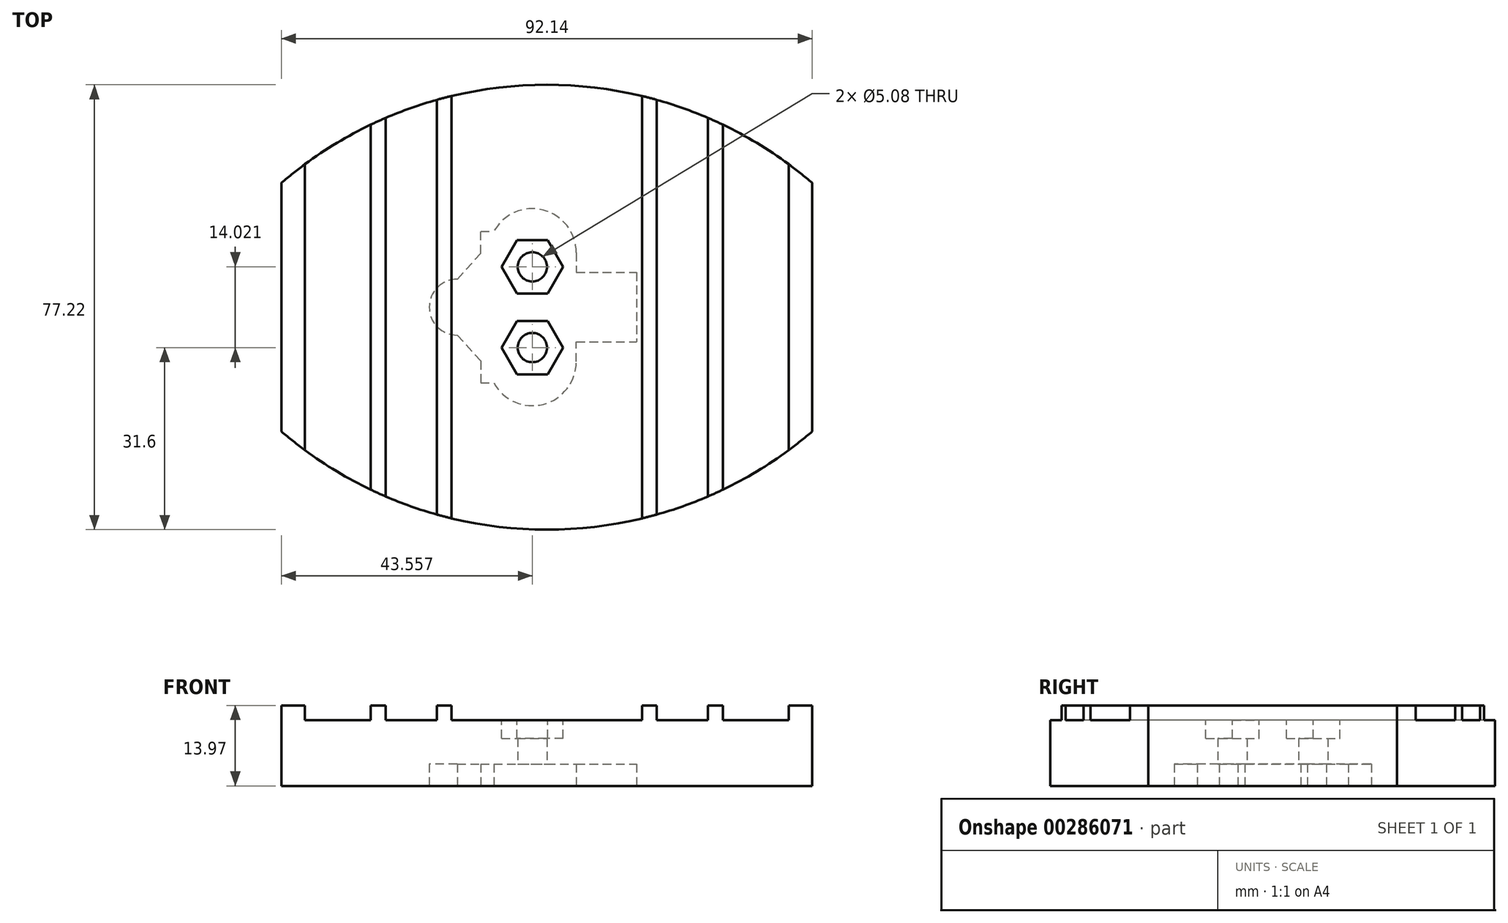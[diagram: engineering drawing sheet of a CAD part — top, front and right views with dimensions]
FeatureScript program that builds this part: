
annotation { "Feature Type Name" : "Feature", "Feature Type Description" : "" }
export const myFeature = defineFeature(function(context is Context, id is Id, definition is map)
    precondition{}
    {
        {
            var Q0;
            Q0=qCreatedBy(makeId("Top.planeOp"),FACE);
            var sketch = newSketch(context, id + "F0", { "sketchPlane" : qUnion([Q0])});
            skLineSegment(sketch, "E0.bottom", {"start": v(46.07, 38.6) * mm, "end": v(-46.07, 38.6) * mm});
            skLineSegment(sketch, "E0.top", {"start": v(46.07, -38.6) * mm, "end": v(-46.07, -38.6) * mm});
            skLineSegment(sketch, "E0.left", {"start": v(46.07, 38.6) * mm, "end": v(46.07, -38.6) * mm});
            skLineSegment(sketch, "E0.right", {"start": v(-46.07, 38.6) * mm, "end": v(-46.07, -38.6) * mm});
            skPoint(sketch, "E0.middle", {"position": v(0, 0) * mm});
            skSolve(sketch);
        }
        {
            var Q0;
            Q0=makeQuery(id+"F0.imprint","IMPRINT",FACE,{"disambiguationData":[TD([[makeQuery(id+"F0.imprint","IMPRINT",EDGE,{"derivedFrom":sQuery(id+"F0.wireOp",EDGE,"E0.bottom")}),1.0]])]});
            extrude(context, id + "F1", {"entities" : qUnion([Q0]), "depth" : 13.97 * mm, "offsetDistance" : 25.4 * mm});
        }
        {
            var Q0;
            Q0=makeQuery(id+"F1.opExtrude","CAP_FACE",FACE,{"disambiguationData":[OSD([sQuery(id+"F0.wireOp",EDGE,"E0.bottom"),sQuery(id+"F0.wireOp",EDGE,"E0.top"),sQuery(id+"F0.wireOp",EDGE,"E0.left"),sQuery(id+"F0.wireOp",EDGE,"E0.right")])],"isStart":false});
            var sketch = newSketch(context, id + "F2", { "sketchPlane" : qUnion([Q0])});
            skLineSegment(sketch, "E1", {"start": v(0, -4.16) * mm, "end": v(0, -123.72) * mm, "construction": true});
            skArc(sketch, "E2", {"start": v(46.07, 21.59) * mm, "mid": v(0, 38.6) * mm, "end": v(-46.07, 21.6) * mm});
            skLineSegment(sketch, "E3", {"start": v(46.07, 0) * mm, "end": v(46.07, 21.59) * mm});
            skPoint(sketch, "E4", {"position": v(-46.07, 21.6) * mm});
            skLineSegment(sketch, "E5", {"start": v(0, -4.16) * mm, "end": v(0, 108.32) * mm, "construction": true});
            skArc(sketch, "E6", {"start": v(-46.07, -21.59) * mm, "mid": v(0, -38.6) * mm, "end": v(46.07, -21.6) * mm});
            skLineSegment(sketch, "E7", {"start": v(-46.07, 0) * mm, "end": v(-46.07, -21.6) * mm});
            skPoint(sketch, "E8", {"position": v(46.07, -21.6) * mm});
            skLineSegment(sketch, "E9", {"start": v(-46.07, 0) * mm, "end": v(-46.07, 21.6) * mm});
            skLineSegment(sketch, "E10", {"start": v(46.07, 0) * mm, "end": v(46.07, -21.6) * mm});
            skSolve(sketch);
        }
        {
            var Q0;
            Q0 = qSketchRegion(id + "F2", true);
            extrude(context, id + "F3", {"entities" : qUnion([Q0]), "operationType" : NewBodyOperationType.INTERSECT, "endBound" : BoundingType.THROUGH_ALL, "oppositeDirection" : true, "depth" : 25.4 * mm});
        }
        {
            var Q0;
            Q0=qCreatedBy(makeId("Front.planeOp"),FACE);
            var sketch = newSketch(context, id + "F4", { "sketchPlane" : qUnion([Q0])});
            skLineSegment(sketch, "E11.bottom", {"start": v(-42, 13.97) * mm, "end": v(-30.57, 13.97) * mm});
            skLineSegment(sketch, "E11.top", {"start": v(-42, 11.43) * mm, "end": v(-30.57, 11.43) * mm});
            skLineSegment(sketch, "E11.left", {"start": v(-42, 13.97) * mm, "end": v(-42, 11.43) * mm});
            skLineSegment(sketch, "E11.right", {"start": v(-30.57, 13.97) * mm, "end": v(-30.57, 11.43) * mm});
            skLineSegment(sketch, "E12.bottom", {"start": v(-27.99, 13.97) * mm, "end": v(-19.1, 13.97) * mm});
            skLineSegment(sketch, "E12.top", {"start": v(-27.99, 11.43) * mm, "end": v(-19.1, 11.43) * mm});
            skLineSegment(sketch, "E12.left", {"start": v(-27.99, 13.97) * mm, "end": v(-27.99, 11.43) * mm});
            skLineSegment(sketch, "E12.right", {"start": v(-19.1, 13.97) * mm, "end": v(-19.1, 11.43) * mm});
            skLineSegment(sketch, "E13.bottom", {"start": v(-16.51, 13.97) * mm, "end": v(16.51, 13.97) * mm});
            skLineSegment(sketch, "E13.top", {"start": v(-16.51, 11.43) * mm, "end": v(16.51, 11.43) * mm});
            skLineSegment(sketch, "E13.left", {"start": v(-16.51, 13.97) * mm, "end": v(-16.51, 11.43) * mm});
            skLineSegment(sketch, "E13.right", {"start": v(16.51, 13.97) * mm, "end": v(16.51, 11.43) * mm});
            skLineSegment(sketch, "E14.bottom", {"start": v(19.1, 13.97) * mm, "end": v(27.99, 13.97) * mm});
            skLineSegment(sketch, "E14.top", {"start": v(19.1, 11.43) * mm, "end": v(27.99, 11.43) * mm});
            skLineSegment(sketch, "E14.left", {"start": v(19.1, 13.97) * mm, "end": v(19.1, 11.43) * mm});
            skLineSegment(sketch, "E14.right", {"start": v(27.99, 13.97) * mm, "end": v(27.99, 11.43) * mm});
            skLineSegment(sketch, "E15.bottom", {"start": v(30.57, 13.97) * mm, "end": v(42, 13.97) * mm});
            skLineSegment(sketch, "E15.top", {"start": v(30.57, 11.43) * mm, "end": v(42, 11.43) * mm});
            skLineSegment(sketch, "E15.left", {"start": v(30.57, 13.97) * mm, "end": v(30.57, 11.43) * mm});
            skLineSegment(sketch, "E15.right", {"start": v(42, 13.97) * mm, "end": v(42, 11.43) * mm});
            skLineSegment(sketch, "E16", {"start": v(0, 11.43) * mm, "end": v(0, 0) * mm});
            skLineSegment(sketch, "E17", {"start": v(-30.57, 12.7) * mm, "end": v(-27.99, 12.7) * mm});
            skLineSegment(sketch, "E18", {"start": v(-19.1, 12.7) * mm, "end": v(-16.51, 12.7) * mm});
            skLineSegment(sketch, "E19", {"start": v(16.51, 12.7) * mm, "end": v(19.1, 12.7) * mm});
            skLineSegment(sketch, "E20", {"start": v(27.99, 12.7) * mm, "end": v(30.57, 12.7) * mm});
            skSolve(sketch);
        }
        {
            var Q0;
            Q0 = qSketchRegion(id + "F4", true);
            extrude(context, id + "F5", {"entities" : qUnion([Q0]), "operationType" : NewBodyOperationType.REMOVE, "endBound" : BoundingType.THROUGH_ALL, "oppositeDirection" : true, "depth" : 25.4 * mm});
        }
        {
            var Q0;
            Q0 = qSketchRegion(id + "F4", true);
            extrude(context, id + "F6", {"entities" : qUnion([Q0]), "operationType" : NewBodyOperationType.REMOVE, "endBound" : BoundingType.THROUGH_ALL, "depth" : 25.4 * mm});
        }
        {
            var Q0;
            Q0=makeQuery(id+"F1.opExtrude","CAP_FACE",FACE,{"disambiguationData":[OSD([sQuery(id+"F0.wireOp",EDGE,"E0.bottom"),sQuery(id+"F0.wireOp",EDGE,"E0.top"),sQuery(id+"F0.wireOp",EDGE,"E0.left"),sQuery(id+"F0.wireOp",EDGE,"E0.right")])],"isStart":true});
            var sketch = newSketch(context, id + "F7", { "sketchPlane" : qUnion([Q0])});
            skLineSegment(sketch, "E21", {"start": v(-50.96, 0) * mm, "end": v(39.64, 0) * mm, "construction": true});
            skArc(sketch, "E22", {"start": v(-20.4, 0) * mm, "mid": v(-18.98, 3.43) * mm, "end": v(-15.55, 4.85) * mm});
            skLineSegment(sketch, "E23", {"start": v(-15.55, 4.85) * mm, "end": v(-11.48, 9.32) * mm});
            skLineSegment(sketch, "E24", {"start": v(-11.48, 9.32) * mm, "end": v(-11.48, 13.13) * mm});
            skLineSegment(sketch, "E25", {"start": v(-11.48, 13.13) * mm, "end": v(-9.2, 13.13) * mm});
            skArc(sketch, "E26", {"start": v(5.1, 9.47) * mm, "mid": v(-2.51, 17.1) * mm, "end": v(-10.13, 9.47) * mm, "construction": true});
            skLineSegment(sketch, "E27", {"start": v(-10.13, 0) * mm, "end": v(-10.13, 9.47) * mm, "construction": true});
            skLineSegment(sketch, "E28", {"start": v(5.1, 9.47) * mm, "end": v(5.1, 6.03) * mm});
            skPoint(sketch, "E29", {"position": v(-2.51, 17.1) * mm});
            skArc(sketch, "E30", {"start": v(5.1, 9.47) * mm, "mid": v(-0.62, 16.86) * mm, "end": v(-9.2, 13.13) * mm});
            skArc(sketch, "E31.MirrorCS", {"start": v(5.1, -9.47) * mm, "mid": v(-0.62, -16.86) * mm, "end": v(-9.2, -13.13) * mm});
            skLineSegment(sketch, "E32.MirrorCS", {"start": v(-11.48, -13.13) * mm, "end": v(-9.2, -13.13) * mm});
            skLineSegment(sketch, "E33.MirrorCS", {"start": v(-11.48, -9.32) * mm, "end": v(-11.48, -13.13) * mm});
            skLineSegment(sketch, "E34.MirrorCS", {"start": v(5.1, -9.47) * mm, "end": v(5.1, -6.03) * mm});
            skLineSegment(sketch, "E35.MirrorCS", {"start": v(-15.55, -4.85) * mm, "end": v(-11.48, -9.32) * mm});
            skArc(sketch, "E36.MirrorCS", {"start": v(-20.4, 0) * mm, "mid": v(-18.98, -3.43) * mm, "end": v(-15.55, -4.85) * mm});
            skLineSegment(sketch, "E37", {"start": v(5.1, 6.03) * mm, "end": v(15.57, 6.03) * mm});
            skLineSegment(sketch, "E38", {"start": v(15.57, 6.03) * mm, "end": v(15.57, 0) * mm});
            skPoint(sketch, "E39.orphan", {"position": v(5.1, 0) * mm});
            skLineSegment(sketch, "E40.MirrorCS", {"start": v(15.57, -6.03) * mm, "end": v(15.57, 0) * mm});
            skLineSegment(sketch, "E41.MirrorCS", {"start": v(5.1, -6.03) * mm, "end": v(15.57, -6.03) * mm});
            skSolve(sketch);
        }
        {
            var Q0;
            Q0 = qSketchRegion(id + "F7", true);
            extrude(context, id + "F8", {"entities" : qUnion([Q0]), "operationType" : NewBodyOperationType.REMOVE, "oppositeDirection" : true, "depth" : 3.8 * mm, "offsetDistance" : 25.4 * mm});
        }
        {
            var Q0;
            Q0=makeQuery(id+"F8.boolean.opBoolean","COPY",FACE,{"derivedFrom":makeQuery(id+"F8.opExtrude","CAP_FACE",FACE,{"disambiguationData":[OSD([sQuery(id+"F7.wireOp",EDGE,"E22"),sQuery(id+"F7.wireOp",EDGE,"E23"),sQuery(id+"F7.wireOp",EDGE,"E24"),sQuery(id+"F7.wireOp",EDGE,"E25"),sQuery(id+"F7.wireOp",EDGE,"E28"),sQuery(id+"F7.wireOp",EDGE,"E30"),sQuery(id+"F7.wireOp",EDGE,"E31.MirrorCS"),sQuery(id+"F7.wireOp",EDGE,"E32.MirrorCS"),sQuery(id+"F7.wireOp",EDGE,"E33.MirrorCS"),sQuery(id+"F7.wireOp",EDGE,"E34.MirrorCS"),sQuery(id+"F7.wireOp",EDGE,"E35.MirrorCS"),sQuery(id+"F7.wireOp",EDGE,"E36.MirrorCS"),sQuery(id+"F7.wireOp",EDGE,"E37"),sQuery(id+"F7.wireOp",EDGE,"E38"),sQuery(id+"F7.wireOp",EDGE,"E40.MirrorCS"),sQuery(id+"F7.wireOp",EDGE,"E41.MirrorCS")])],"isStart":false})});
            var sketch = newSketch(context, id + "F9", { "sketchPlane" : qUnion([Q0])});
            skArc(sketch, "E42.0", {"start": v(5.1, -9.47) * mm, "mid": v(-0.62, -16.86) * mm, "end": v(-9.2, -13.13) * mm, "construction": true});
            skLineSegment(sketch, "E42.1", {"start": v(5.1, -9.47) * mm, "end": v(5.1, -6.03) * mm, "construction": true});
            skLineSegment(sketch, "E42.2", {"start": v(5.1, 9.47) * mm, "end": v(5.1, 6.03) * mm, "construction": true});
            skArc(sketch, "E42.3", {"start": v(5.1, 9.47) * mm, "mid": v(-0.62, 16.86) * mm, "end": v(-9.2, 13.13) * mm, "construction": true});
            skCircle(sketch, "E43", {"center": v(-2.51, -7.01) * mm, "radius": 2.54 * mm});
            skCircle(sketch, "E44", {"center": v(-2.51, 7.01) * mm, "radius": 2.54 * mm});
            skLineSegment(sketch, "E45", {"start": v(-2.51, -9.47) * mm, "end": v(-2.51, -7.01) * mm, "construction": true});
            skLineSegment(sketch, "E46", {"start": v(-2.51, 7.01) * mm, "end": v(-2.51, 9.47) * mm, "construction": true});
            skSolve(sketch);
        }
        {
            var Q0;
            Q0 = qSketchRegion(id + "F9", true);
            extrude(context, id + "F10", {"entities" : qUnion([Q0]), "operationType" : NewBodyOperationType.REMOVE, "oppositeDirection" : true, "depth" : 25.4 * mm, "offsetDistance" : 25.4 * mm});
        }
        {
            var Q0;
            {var subQ0=sQuery(id+"F4.wireOp",EDGE,"E13.top");Q0=makeQuery(id+"F6.boolean.opBoolean","MERGE",FACE,{"derivedFrom":[makeQuery(id+"F5.boolean.opBoolean","COPY",FACE,{"derivedFrom":makeQuery(id+"F5.opExtrude","SWEPT_FACE",FACE,{"disambiguationData":[OSD([subQ0])]})}),makeQuery(id+"F6.opExtrude","SWEPT_FACE",FACE,{"disambiguationData":[OSD([subQ0])]})]});}
            var sketch = newSketch(context, id + "F11", { "sketchPlane" : qUnion([Q0])});
            skCircle(sketch, "E47.0", {"center": v(-2.51, -7.01) * mm, "radius": 2.54 * mm, "construction": true});
            skCircle(sketch, "E47.1", {"center": v(-2.51, 7.01) * mm, "radius": 2.54 * mm, "construction": true});
            skCircle(sketch, "E48.cCircle", {"center": v(-2.51, -7.01) * mm, "radius": 4.64 * mm, "construction": true});
            skLineSegment(sketch, "E48.0", {"start": v(-7.87, -7.01) * mm, "end": v(-5.19, -2.37) * mm});
            skLineSegment(sketch, "E48.1", {"start": v(-5.19, -2.37) * mm, "end": v(0.16, -2.37) * mm});
            skLineSegment(sketch, "E48.2", {"start": v(0.16, -2.37) * mm, "end": v(2.84, -7.01) * mm});
            skLineSegment(sketch, "E48.3", {"start": v(2.84, -7.01) * mm, "end": v(0.16, -11.65) * mm});
            skLineSegment(sketch, "E48.4", {"start": v(0.16, -11.65) * mm, "end": v(-5.19, -11.65) * mm});
            skLineSegment(sketch, "E48.5", {"start": v(-5.19, -11.65) * mm, "end": v(-7.87, -7.01) * mm});
            skPoint(sketch, "E48.0.midPoint", {"position": v(-6.53, -4.7) * mm});
            skCircle(sketch, "E49.cCircle", {"center": v(-2.51, 7.01) * mm, "radius": 4.64 * mm, "construction": true});
            skLineSegment(sketch, "E49.0", {"start": v(-5.19, 11.65) * mm, "end": v(0.16, 11.65) * mm});
            skLineSegment(sketch, "E49.1", {"start": v(0.16, 11.65) * mm, "end": v(2.84, 7.01) * mm});
            skLineSegment(sketch, "E49.2", {"start": v(2.84, 7.01) * mm, "end": v(0.16, 2.37) * mm});
            skLineSegment(sketch, "E49.3", {"start": v(0.16, 2.37) * mm, "end": v(-5.19, 2.37) * mm});
            skLineSegment(sketch, "E49.4", {"start": v(-5.19, 2.37) * mm, "end": v(-7.87, 7.01) * mm});
            skLineSegment(sketch, "E49.5", {"start": v(-7.87, 7.01) * mm, "end": v(-5.19, 11.65) * mm});
            skPoint(sketch, "E49.0.midPoint", {"position": v(-2.51, 11.65) * mm});
            skSolve(sketch);
        }
        {
            var Q0;
            Q0 = qSketchRegion(id + "F11", true);
            extrude(context, id + "F12", {"entities" : qUnion([Q0]), "operationType" : NewBodyOperationType.REMOVE, "oppositeDirection" : true, "depth" : 3.17 * mm, "offsetDistance" : 25.4 * mm});
        }
    });
